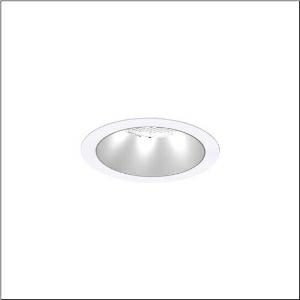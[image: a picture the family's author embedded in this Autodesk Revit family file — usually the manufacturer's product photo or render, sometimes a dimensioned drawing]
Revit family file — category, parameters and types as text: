
# Revit family: lunis_21_l_51db19td91c
name_source: partatom
category: Lighting Fixtures
units: mm (PartAtom-declared; Revit-internal decimal feet)

## family parameters
Cut with Voids When Loaded = No
Host = Face
Light Source = No
Part Type = Normal
Room Calculation Point = No
Round Connector Dimension = Use Diameter
Shared = No

## types (1)
- --- (1 x LED 3000 K ... 6500 K, 3900 lm, 25.4 W, 4000K)
    Apparent Load = 25 VA
    CIE Flux Codes = 91 99 100 100 100
    Color Rendering = 80
    Color Temperature = 4000K
    Default Elevation = 1800 mm
    Description = Lunis 21,  L, downlight, light control with lens, of PMMA, anti glare with reflector, of aluminium, matt, light emission: direct distribution, LED rated luminous flux: 3.900lm, light colour: 8tw, with terminal, 5-pole, mains connection: 220..240V, AC/DC, 0/50..60Hz, housing, round, of diecast aluminium, traffic white (RAL 9016), diameter: 165mm, clamping range: 1..40mm, protection rating (complete): IP20, protection rating (on room side): IP54, insulation class (complete): insulation class II (safety insulation), certification: CE, impact resistance: IK03, packaging unit: 1 piece
    Height = 0 mm  [stored 0 ft]
    Lamp = 1 x LED 3000 K ... 6500 K
    Lamp Light Flux = 3900 lm
    Lamp Power = 25.4 W
    Lamp count = 1
    Length = 165 mm
    Luminous efficacy = 154 lm/W
    Manufacturer = Siteco
    ModVariant = No
    Model = 51DB19TD91C
    Mounting Place = Ceiling
    Mounting Type = Recessed
    Number of Poles = 1
    OnlyDefault = Yes
    Power Factor = 1
    Product Name = Lunis 21 L
    Product group = downlight
    ProductGroupID = 400
    Protection Class = Protection class II
    Protection Degree = IP 20
    RLX_Detail_Level = 1
    RLX_Emergency_Light_Flux = 0 lm
    RLX_Emergency_Type = 0
    RLX_Emergency_Type_DB = No
    RlxData = <blob elided: 15149 chars, md5=c1c6e62b>
    Socket = socket
    Standby Power = 0 W
    System Light Flux = 3900 lm
    System Power = 25 W
    Type Comments = individual setting: CCT=4000K, colour temperature 4000K, luminous flux: 100 % | (ON | ON | OFF | OFF) | 700 mA
    Type Image = l_1291096.jpg
    URL = http://relux.com
    VarID = @adj_018844
    Voltage = 0 V
    Weight = 0.00 kg
    Width = 0 mm  [stored 0 ft]

note: [stored X ft] marks values corroborated as IEEE doubles in the binary element streams (Revit-internal decimal feet)

## geometry (parser evidence)
native form markers: Sweep x9
no freeform markers — native parametric forms only
